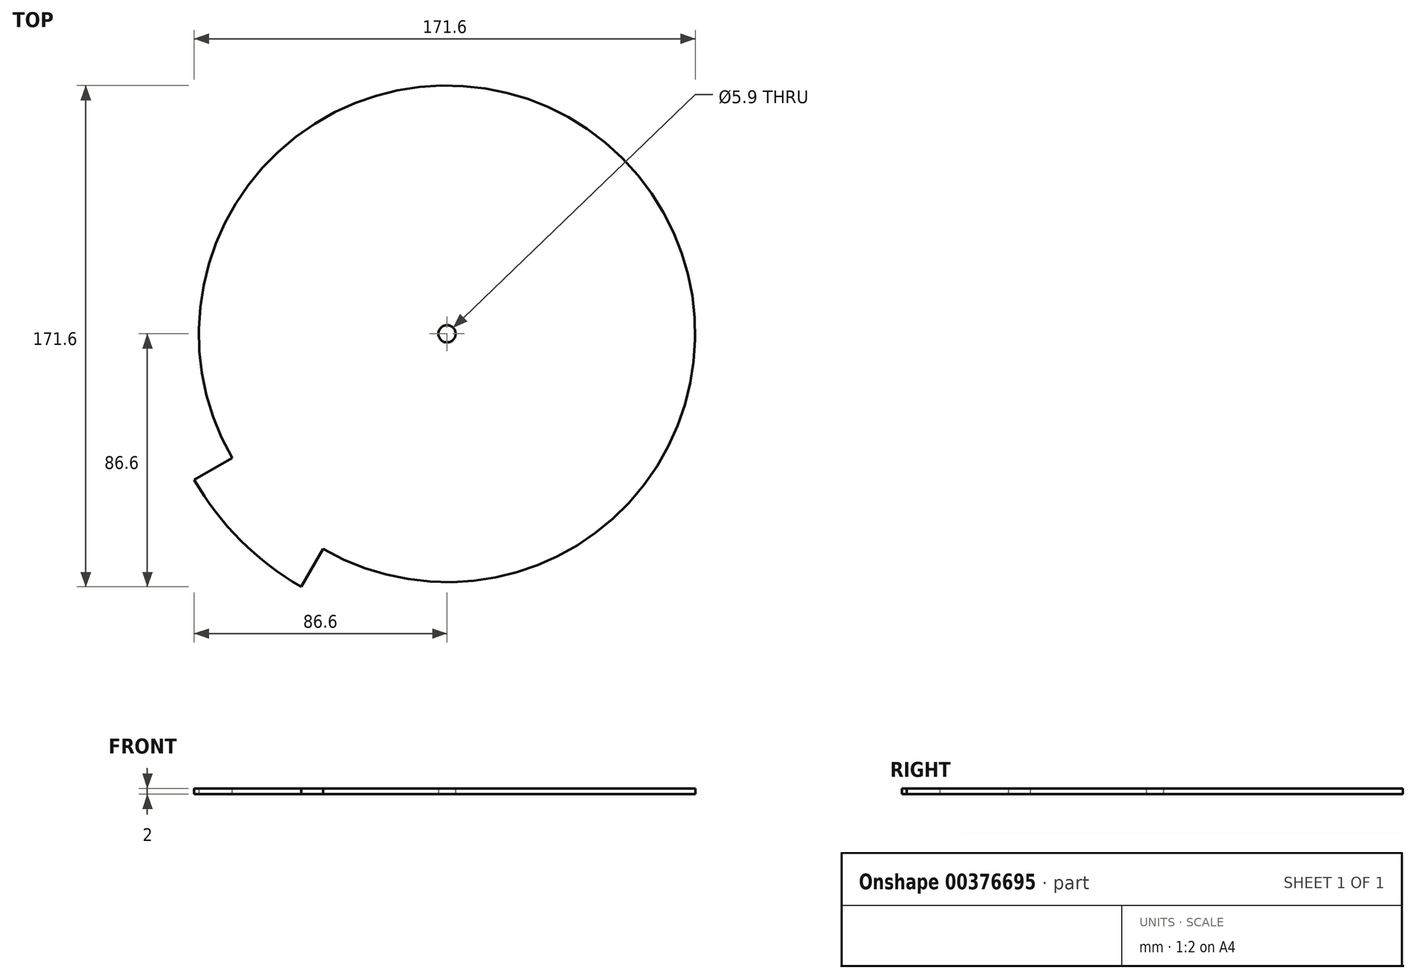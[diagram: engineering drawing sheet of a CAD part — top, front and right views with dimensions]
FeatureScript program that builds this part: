
annotation { "Feature Type Name" : "Feature", "Feature Type Description" : "" }
export const myFeature = defineFeature(function(context is Context, id is Id, definition is map)
    precondition{}
    {
        {
            var Q0;
            Q0=qCreatedBy(makeId("Top.planeOp"),FACE);
            var sketch = newSketch(context, id + "F0", { "sketchPlane" : qUnion([Q0])});
            skCircle(sketch, "E0", {"center": v(0, 0) * mm, "radius": 85 * mm});
            skSolve(sketch);
        }
        {
            var Q0;
            Q0 = qSketchRegion(id + "F0", true);
            var Q1;
            {var subQ3=sQuery(id+"F0.wireOp",EDGE,"SQs7pcE5-xKAt-AdiO-ETJP-9d5siaddILx5");Q1=makeQuery(id+"F0.imprint","IMPRINT",FACE,{"disambiguationData":[TD([[makeQuery(id+"F0.imprint","IMPRINT",EDGE,{"derivedFrom":subQ3}),-1.0]])]});}
            var Q2;
            {var subQ3=sQuery(id+"F0.wireOp",EDGE,"SQs7pcE5-xKAt-AdiO-ETJP-9d5siaddILx5");Q2=makeQuery(id+"F0.imprint","IMPRINT",FACE,{"disambiguationData":[TD([[makeQuery(id+"F0.imprint","IMPRINT",EDGE,{"derivedFrom":subQ3}),1.0]])]});}
            var Q3;
            {var subQ0=sQuery(id+"F0.wireOp",EDGE,"O7SK3Dak-j1g5-xDk8-UPqP-V7o3w3lRkpe8");Q3=makeQuery(id+"F0.imprint","IMPRINT",FACE,{"disambiguationData":[TD([[makeQuery(id+"F0.imprint","IMPRINT",EDGE,{"derivedFrom":subQ0}),1.0]])]});}
            var Q4;
            {var subQ3=sQuery(id+"F0.wireOp",EDGE,"O7SK3Dak-j1g5-xDk8-UPqP-V7o3w3lRkpe8");Q4=makeQuery(id+"F0.imprint","IMPRINT",FACE,{"disambiguationData":[TD([[makeQuery(id+"F0.imprint","IMPRINT",EDGE,{"derivedFrom":subQ3}),-1.0]])]});}
            extrude(context, id + "F1", {"entities" : qUnion([Q0, Q1, Q2, Q3, Q4]), "depth" : 2 * mm});
        }
        {
            var Q0;
            Q0=makeQuery(id+"F1.opExtrude","CAP_FACE",FACE,{"disambiguationData":[OSD([sQuery(id+"F0.wireOp",EDGE,"E0")])],"isStart":false});
            var sketch = newSketch(context, id + "F2", { "sketchPlane" : qUnion([Q0])});
            skLineSegment(sketch, "E1", {"start": v(-73.61, -42.5) * mm, "end": v(-86.6, -50) * mm});
            skLineSegment(sketch, "E2", {"start": v(-42.5, -73.61) * mm, "end": v(-50, -86.6) * mm});
            skArc(sketch, "E3", {"start": v(-86.6, -50) * mm, "mid": v(-70.71, -70.71) * mm, "end": v(-50, -86.6) * mm});
            skArc(sketch, "E4", {"start": v(-73.61, -42.5) * mm, "mid": v(-60.1, -60.1) * mm, "end": v(-42.5, -73.61) * mm});
            skSolve(sketch);
        }
        {
            var Q0;
            {var subQ0=sQuery(id+"F2.wireOp",EDGE,"E1");Q0=makeQuery(id+"F2.imprint","IMPRINT",FACE,{"disambiguationData":[TD([[makeQuery(id+"F2.imprint","IMPRINT",EDGE,{"derivedFrom":subQ0}),1.0]])]});}
            extrude(context, id + "F3", {"entities" : qUnion([Q0]), "operationType" : NewBodyOperationType.ADD, "oppositeDirection" : true, "depth" : 2 * mm});
        }
        {
            var Q0;
            {var subQ0=sQuery(id+"F2.wireOp",EDGE,"E4");var subQ1=sQuery(id+"F2.wireOp",EDGE,"E3");var subQ2=sQuery(id+"F2.wireOp",EDGE,"E2");var subQ3=sQuery(id+"F2.wireOp",EDGE,"E1");Q0=makeQuery(id+"FPGSIWIwRmekZ3o_1.1.FxgF0eQ84fsk9A0_1.1.F3.boolean.opBoolean","MERGE",FACE,{"derivedFrom":[makeQuery(id+"FPGSIWIwRmekZ3o_1.1.F3.boolean.opBoolean","MERGE",FACE,{"derivedFrom":[makeQuery(id+"FxgF0eQ84fsk9A0_1.1.F3.boolean.opBoolean","MERGE",FACE,{"derivedFrom":[makeQuery(id+"F3.opExtrude","CAP_FACE",FACE,{"disambiguationData":[OSD([subQ3,subQ2,subQ1,subQ0])],"isStart":false}),makeQuery(id+"FxgF0eQ84fsk9A0_1.1.F3.opExtrude","CAP_FACE",FACE,{"disambiguationData":[OSD([subQ3,subQ2,subQ1,subQ0])],"isStart":false})]}),makeQuery(id+"FPGSIWIwRmekZ3o_1.1.F3.opExtrude","CAP_FACE",FACE,{"disambiguationData":[OSD([subQ3,subQ2,subQ1,subQ0])],"isStart":false})]}),makeQuery(id+"FPGSIWIwRmekZ3o_1.1.FxgF0eQ84fsk9A0_1.1.F3.opExtrude","CAP_FACE",FACE,{"disambiguationData":[OSD([subQ3,subQ2,subQ1,subQ0])],"isStart":false})]});}
            var sketch = newSketch(context, id + "F4", { "sketchPlane" : qUnion([Q0])});
            skCircle(sketch, "E5", {"center": v(0, 0) * mm, "radius": 2.95 * mm});
            skSolve(sketch);
        }
        {
            var Q0;
            Q0 = qSketchRegion(id + "F4", true);
            extrude(context, id + "F5", {"entities" : qUnion([Q0]), "operationType" : NewBodyOperationType.REMOVE, "oppositeDirection" : true, "depth" : 25 * mm});
        }
    });
